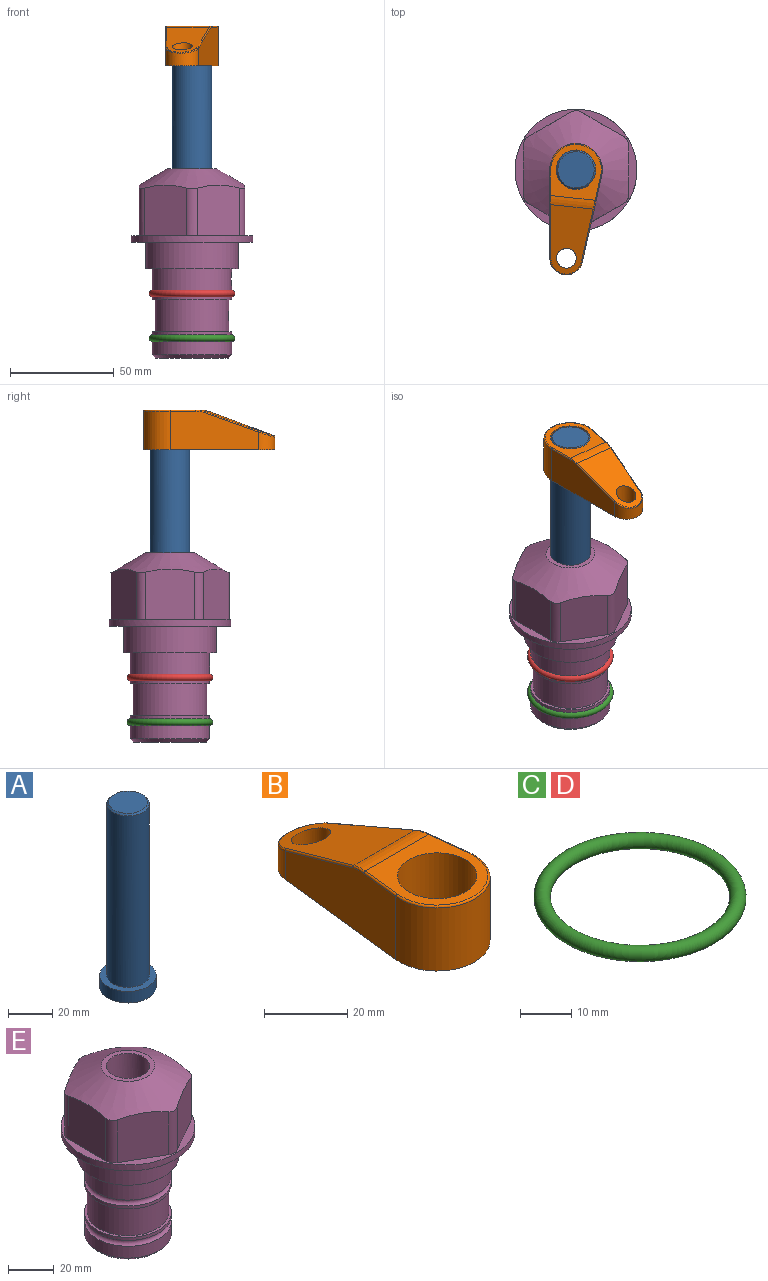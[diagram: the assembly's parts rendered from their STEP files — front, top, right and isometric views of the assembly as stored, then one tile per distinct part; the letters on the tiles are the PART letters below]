
ASSEMBLY  parts=5 mates=3
PART A: 6 faces, bbox 25.4x25.4x101.6 mm
  f0: plane 17.46x17.46mm, normal (0,0,1), area 239.5mm2, adj f5
  f1: plane 25.4x25.4mm, normal (0,0,-1), area 506.7mm2, adj f2
  f2: cylinder r=12.7mm len=25.4mm, axis (0,0,1), area 506.7mm2, adj f1,f3
  f3: plane 25.4x25.4mm, normal (0,0,1), area 221.7mm2, adj f2,f4
  f4: cylinder r=9.53mm len=94.46mm, axis (0,0,1), area 5653mm2, adj f3,f5
  f5: cone r=8.73mm half-angle=45deg, axis (0,0,-1), area 64.4mm2, adj f0,f4
PART B: 44 faces, bbox 27.5x64.5x19.1 mm
  f0: plane 2.3x0.95mm, normal (0,0,-1), area 1mm2, adj f25,f30,f34
  f1: plane 63.5x25.4mm, normal (0,0,-1), area 561.7mm2, adj f2,f3,f4,f5,f6,f7,f19,f20
  f2: cylinder r=12.7mm len=25.4mm, axis (0,0,-1), area 792.2mm2, adj f1,f3,f5,f13
  f3: plane 42.33x18.54mm, normal (0.99,0.11,0), area 647mm2, adj f1,f2,f4,f11,f12,f14
  f4: cylinder r=7.94mm len=15.78mm, axis (0,0,-1), area 158.6mm2, adj f1,f3,f5,f16
  f5: plane 42.33x18.54mm, normal (-0.99,0.11,0), area 647mm2, adj f1,f2,f4,f15,f17,f18
  f6: cylinder r=9.53mm len=19.05mm, axis (0,0,-1), area 1140.1mm2, adj f1,f8
  f7: cylinder r=4.76mm len=10.98mm, axis (0,0,-1), area 276.1mm2, adj f1,f9
  f8: plane 25.83x24.38mm, normal (0,0,1), area 262.2mm2, adj f6,f10,f11,f13,f15
  f9: plane 32.49x20.55mm, normal (0,0.34,0.94), area 489.9mm2, adj f7,f10,f14,f16,f18
  f10: cylinder r=12.7mm len=21.49mm, axis (-1,0,0), area 93.2mm2, adj f8,f9,f12,f17
  f11: cylinder r=0.51mm len=12.34mm, axis (0.11,-0.99,0), area 9.9mm2, adj f3,f8,f12,f13
  f12: bspline ~7.62x1.64mm, area 3.5mm2, adj f3,f10,f11,f14
  f13: torus R=12.19mm, axis (0,0,1), area 33.6mm2, adj f2,f8,f11,f15
  f14: cylinder r=0.51mm len=26.01mm, axis (0.1,-0.93,0.34), area 21.6mm2, adj f3,f9,f12,f16
  f15: cylinder r=0.51mm len=12.34mm, axis (0.11,0.99,0), area 9.9mm2, adj f5,f8,f13,f17
  f16: bspline ~15.78x7.05mm, area 15.7mm2, adj f4,f9,f14,f18
  f17: bspline ~7.62x1.64mm, area 3.5mm2, adj f5,f10,f15,f18
  f18: cylinder r=0.51mm len=26.01mm, axis (0.1,0.93,-0.34), area 21.6mm2, adj f5,f9,f16,f17
  f19: plane 21.6x14.29mm, normal (-0.99,-0.11,0), area 242.6mm2, adj f1,f26,f28,f34,f36,f38
  f20: plane 21.6x14.29mm, normal (0.99,-0.11,0), area 242.6mm2, adj f1,f27,f29,f37,f39,f41
  f21: cylinder r=12.7mm len=14.29mm, axis (0,0,-1), area 173.2mm2, adj f1,f26,f27,f30,f31,f33
  f22: cylinder r=7.94mm len=7.63mm, axis (0,0,-1), area 53.8mm2, adj f1,f28,f29,f42
  f23: plane 2.3x0.95mm, normal (0,0,-1), area 1mm2, adj f25,f33,f37
  f24: plane 17.94x12.32mm, normal (0,-0.34,-0.94), area 191.2mm2, adj f25,f38,f41,f42
  f25: cylinder r=9.53mm len=12.93mm, axis (-1,0,0), area 37.5mm2, adj f0,f23,f24,f31,f36,f39
  f26: cylinder r=1.59mm len=14.29mm, axis (0,0,-1), area 49mm2, adj f1,f19,f21,f32
  f27: cylinder r=1.59mm len=14.29mm, axis (0,0,-1), area 49mm2, adj f1,f20,f21,f35
  f28: cylinder r=1.59mm len=7.28mm, axis (0,0,-1), area 22.1mm2, adj f1,f19,f22,f40
  f29: cylinder r=1.59mm len=7.28mm, axis (0,0,-1), area 22.1mm2, adj f1,f20,f22,f43
  f30: torus R=14.29mm, axis (0,0,1), area 5.8mm2, adj f0,f21,f31,f32
  f31: bspline ~11.06x2.73mm, area 20.8mm2, adj f21,f25,f30,f33
  f32: sphere r=1.59mm, area 5.4mm2, adj f26,f30,f34
  f33: torus R=14.29mm, axis (0,0,1), area 5.8mm2, adj f21,f23,f31,f35
  f34: cylinder r=1.59mm len=1.68mm, axis (-0.11,0.99,0), area 2.4mm2, adj f0,f19,f32,f36
  f35: sphere r=1.59mm, area 5.4mm2, adj f27,f33,f37
  f36: bspline ~5.82x2.33mm, area 7.7mm2, adj f19,f25,f34,f38
  f37: cylinder r=1.59mm len=1.68mm, axis (0.11,0.99,0), area 2.4mm2, adj f20,f23,f35,f39
  f38: cylinder r=1.59mm len=18.33mm, axis (0.1,-0.93,0.34), area 46.7mm2, adj f19,f24,f36,f40
  f39: bspline ~5.82x2.33mm, area 7.7mm2, adj f20,f25,f37,f41
  f40: sphere r=1.59mm, area 3.6mm2, adj f28,f38,f42
  f41: cylinder r=1.59mm len=18.33mm, axis (0.1,0.93,-0.34), area 46.7mm2, adj f20,f24,f39,f43
  f42: bspline ~8.31x1.84mm, area 15.3mm2, adj f22,f24,f40,f43
  f43: sphere r=1.59mm, area 3.6mm2, adj f29,f41,f42
PART C: 1 faces, bbox 44.7x44.7x3.2 mm
  f0: torus R=19.05mm, axis (0,0,1), area 1193.9mm2
PART D: same geometry as C
PART E: 36 faces, bbox 58.7x58.7x91.2 mm
  f0: cylinder r=17.78mm len=35.56mm, axis (0,0,1), area 1670.8mm2, adj f23,f24,f31
  f1: cylinder r=19.05mm len=38.1mm, axis (0,0,1), area 1191.9mm2, adj f26,f27,f30
  f2: plane 58.66x58.66mm, normal (0,0,-1), area 1150.6mm2, adj f3,f28
  f3: cylinder r=29.33mm len=58.66mm, axis (0,0,-1), area 585.1mm2, adj f2,f4
  f4: plane 58.66x58.66mm, normal (0,0,1), area 475.9mm2, adj f3,f5,f6,f7,f8,f9,f10,f11
  f5: plane 24.5x20.32mm, normal (-0.5,0.87,0), area 562.8mm2, adj f4,f15,f16,f17
  f6: plane 24.5x20.32mm, normal (0.5,0.87,0), area 562.8mm2, adj f4,f14,f15,f17
  f7: plane 24.5x23.48mm, normal (1,0,0), area 562.8mm2, adj f4,f13,f14,f17
  f8: plane 24.5x20.32mm, normal (0.5,-0.87,0), area 562.8mm2, adj f4,f12,f13,f17
  f9: plane 24.5x20.32mm, normal (-0.5,-0.87,0), area 562.8mm2, adj f4,f11,f12,f17
  f10: plane 24.5x23.48mm, normal (-1,0,0), area 562.8mm2, adj f4,f11,f16,f17
  f11: cylinder r=5.08mm len=23.01mm, axis (0,0,-1), area 121.2mm2, adj f4,f9,f10,f17
  f12: cylinder r=5.08mm len=23.01mm, axis (0,0,-1), area 121.2mm2, adj f4,f8,f9,f17
  f13: cylinder r=5.08mm len=23.01mm, axis (0,0,-1), area 121.2mm2, adj f4,f7,f8,f17
  f14: cylinder r=5.08mm len=23.01mm, axis (0,0,-1), area 121.2mm2, adj f4,f6,f7,f17
  f15: cylinder r=5.08mm len=23.01mm, axis (0,0,-1), area 121.2mm2, adj f4,f5,f6,f17
  f16: cylinder r=5.08mm len=23.01mm, axis (0,0,-1), area 121.2mm2, adj f4,f5,f10,f17
  f17: cone r=11.73mm half-angle=60deg, axis (0,0,-1), area 2071.8mm2, adj f5,f6,f7,f8,f9,f10,f11,f12
  f18: plane 23.46x23.46mm, normal (0,0,1), area 147.4mm2, adj f17,f35
  f19: plane 34.93x34.93mm, normal (0,0,-1), area 958mm2, adj f29
  f20: cylinder r=19.05mm len=38.1mm, axis (0,0,1), area 760.1mm2, adj f21,f29
  f21: torus R=19.05mm, axis (0,0,1), area 565.3mm2, adj f20,f22
  f22: cylinder r=19.05mm len=38.1mm, axis (0,0,1), area 190mm2, adj f21,f23
  f23: plane 38.1x38.1mm, normal (0,0,1), area 146.9mm2, adj f0,f22
  f24: plane 38.1x38.1mm, normal (0,0,-1), area 146.9mm2, adj f0,f25
  f25: cylinder r=19.05mm len=38.1mm, axis (0,0,1), area 190mm2, adj f24,f26
  f26: torus R=19.05mm, axis (0,0,1), area 565.3mm2, adj f1,f25
  f27: plane 44.45x44.45mm, normal (0,0,-1), area 411.7mm2, adj f1,f28
  f28: cylinder r=22.23mm len=44.45mm, axis (0,0,1), area 1773.5mm2, adj f2,f27
  f29: cone r=19.05mm half-angle=45deg, axis (0,0,1), area 257.5mm2, adj f19,f20
  f30: cylinder r=3.17mm len=6.75mm, axis (-1,0,0), area 128mm2, adj f1,f33
  f31: cylinder r=3.17mm len=6.35mm, axis (-1,0,0), area 102.5mm2, adj f0,f33
  f32: plane 25.4x25.4mm, normal (0,0,1), area 506.7mm2, adj f33
  f33: cylinder r=12.7mm len=66.42mm, axis (0,0,-1), area 5236.2mm2, adj f30,f31,f32,f34
  f34: cone r=9.53mm half-angle=30deg, axis (0,0,-1), area 443.4mm2, adj f33,f35
  f35: cylinder r=9.53mm len=19.05mm, axis (0,0,-1), area 849mm2, adj f18,f34
PLACE A rot(axis=(0,0,-1),96.2deg) t=(0,0,30.57)mm
PLACE B rot(axis=(0,0,1),173.8deg) t=(0,0,85.18)mm
PLACE C t=(0,0,-21.59)mm
PLACE D at identity
PLACE E at identity fixed
MATE fastened C.f0 <-> E.f0  axis (0,0,1) through (0,0,-46.1)mm
MATE cylindrical A.f2 <-> E.f0  axis (0,0,1) through (0,0,56.21)mm
MATE fastened B.f2 <-> A.f2  axis (0,0,1) through (0,0,104.23)mm
